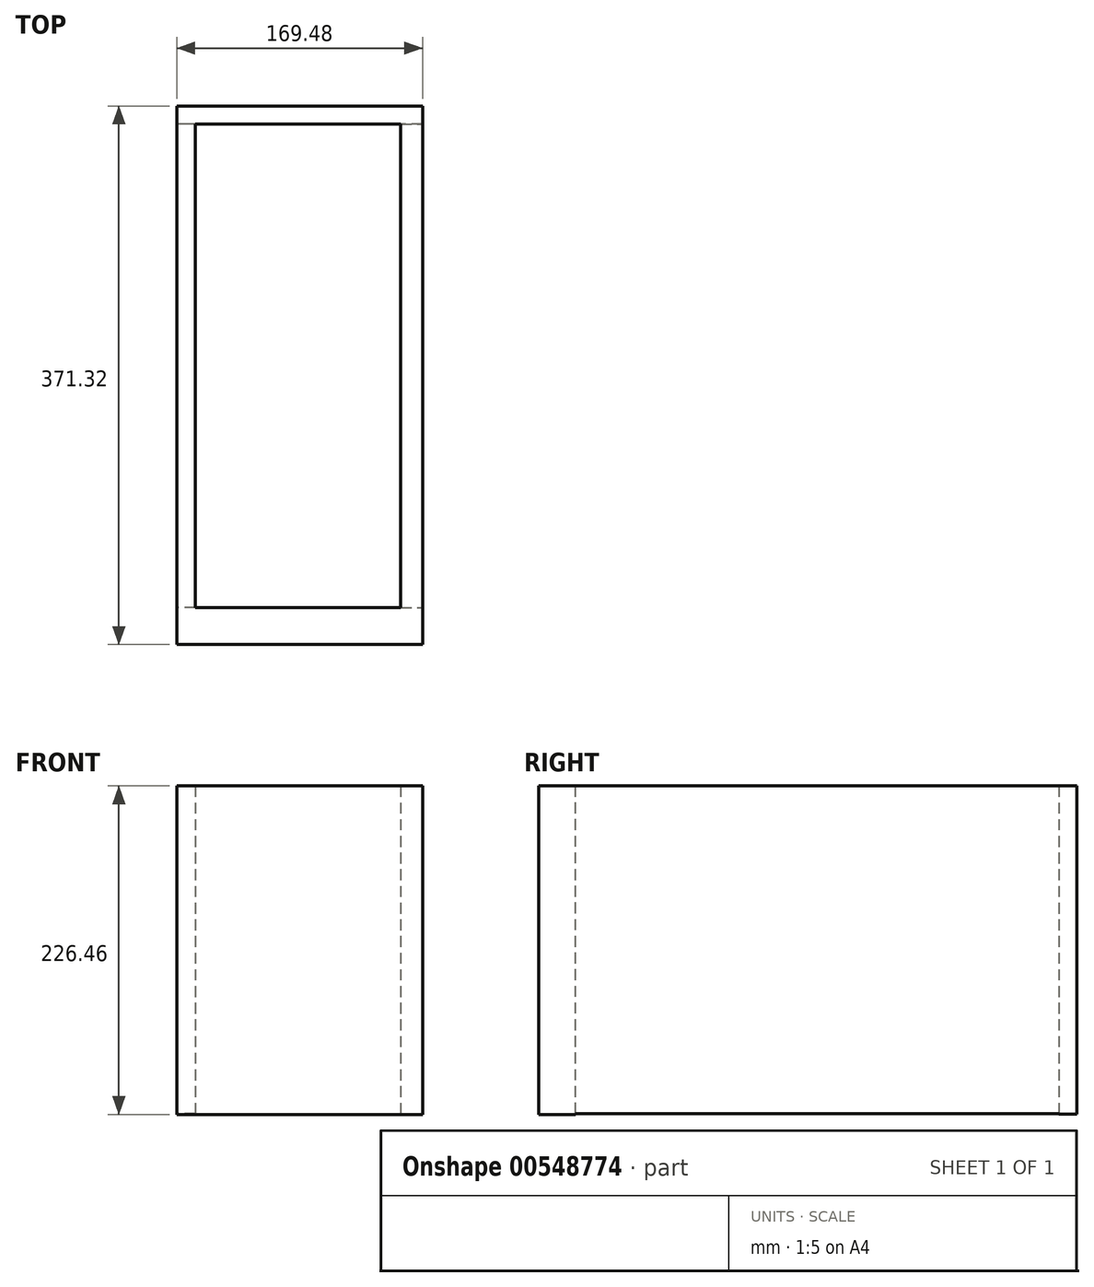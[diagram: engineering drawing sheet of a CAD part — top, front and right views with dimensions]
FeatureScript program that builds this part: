
annotation { "Feature Type Name" : "Feature", "Feature Type Description" : "" }
export const myFeature = defineFeature(function(context is Context, id is Id, definition is map)
    precondition{}
    {
        {
            var Q0;
            Q0=qCreatedBy(makeId("Front.planeOp"),FACE);
            var sketch = newSketch(context, id + "F0", { "sketchPlane" : qUnion([Q0])});
            skLineSegment(sketch, "E0.bottom", {"start": v(-84.74, -113.23) * mm, "end": v(84.74, -113.23) * mm});
            skLineSegment(sketch, "E0.top", {"start": v(-84.74, 113.23) * mm, "end": v(84.74, 113.23) * mm});
            skLineSegment(sketch, "E0.left", {"start": v(-84.74, -113.23) * mm, "end": v(-84.74, 113.23) * mm});
            skLineSegment(sketch, "E0.right", {"start": v(84.74, -113.23) * mm, "end": v(84.74, 113.23) * mm});
            skPoint(sketch, "E0.middle", {"position": v(0, 0) * mm});
            skSolve(sketch);
        }
        {
            var Q0;
            Q0=makeQuery(id+"F0.imprint","IMPRINT",FACE,{"disambiguationData":[TD([[makeQuery(id+"F0.imprint","IMPRINT",EDGE,{"derivedFrom":sQuery(id+"F0.wireOp",EDGE,"E0.bottom")}),1.0]])]});
            extrude(context, id + "F1", {"entities" : qUnion([Q0]), "depth" : 25.4 * mm, "offsetDistance" : 25.4 * mm});
        }
        {
            var Q0;
            Q0=makeQuery(id+"F1.opExtrude","SWEPT_FACE",FACE,{"disambiguationData":[OSD([sQuery(id+"F0.wireOp",EDGE,"E0.right")])]});
            var sketch = newSketch(context, id + "F2", { "sketchPlane" : qUnion([Q0])});
            skLineSegment(sketch, "E1.bottom", {"start": v(0, 113.23) * mm, "end": v(345.92, 113.23) * mm});
            skLineSegment(sketch, "E1.top", {"start": v(0, -112.63) * mm, "end": v(345.92, -112.63) * mm});
            skLineSegment(sketch, "E1.left", {"start": v(0, 113.23) * mm, "end": v(0, -112.63) * mm});
            skLineSegment(sketch, "E1.right", {"start": v(345.92, 113.23) * mm, "end": v(345.92, -112.63) * mm});
            skSolve(sketch);
        }
        {
            var Q0;
            Q0=makeQuery(id+"F1.opExtrude","SWEPT_FACE",FACE,{"disambiguationData":[OSD([sQuery(id+"F0.wireOp",EDGE,"E0.left")])]});
            var sketch = newSketch(context, id + "F3", { "sketchPlane" : qUnion([Q0])});
            skLineSegment(sketch, "E2.bottom", {"start": v(25.4, 113.23) * mm, "end": v(-345.58, 113.23) * mm});
            skLineSegment(sketch, "E2.top", {"start": v(25.4, -112.66) * mm, "end": v(-345.58, -112.66) * mm});
            skLineSegment(sketch, "E2.left", {"start": v(25.4, 113.23) * mm, "end": v(25.4, -112.66) * mm});
            skLineSegment(sketch, "E2.right", {"start": v(-345.58, 113.23) * mm, "end": v(-345.58, -112.66) * mm});
            skSolve(sketch);
        }
        {
            var Q0;
            {var subQ3=sQuery(id+"F3.wireOp",EDGE,"E2.right");Q0=makeQuery(id+"F3.imprint","IMPRINT",FACE,{"disambiguationData":[TD([[makeQuery(id+"F3.imprint","IMPRINT",EDGE,{"derivedFrom":subQ3}),1.0]])]});}
            extrude(context, id + "F4", {"entities" : qUnion([Q0]), "operationType" : NewBodyOperationType.ADD, "oppositeDirection" : true, "depth" : 12.88 * mm, "offsetDistance" : 25.4 * mm});
        }
        {
            var Q0;
            Q0=makeQuery(id+"F2.imprint","IMPRINT",FACE,{"disambiguationData":[TD([[makeQuery(id+"F2.imprint","IMPRINT",EDGE,{"derivedFrom":sQuery(id+"F2.wireOp",EDGE,"E1.bottom")}),-1.0]])]});
            extrude(context, id + "F5", {"entities" : qUnion([Q0]), "operationType" : NewBodyOperationType.ADD, "oppositeDirection" : true, "depth" : 15.04 * mm, "offsetDistance" : 25.4 * mm});
        }
        {
            var Q0;
            Q0=makeQuery(id+"F5.opExtrude","SWEPT_FACE",FACE,{"disambiguationData":[OSD([sQuery(id+"F2.wireOp",EDGE,"E1.right")])]});
            var sketch = newSketch(context, id + "F6", { "sketchPlane" : qUnion([Q0])});
            skLineSegment(sketch, "E3.bottom", {"start": v(-84.74, 113.23) * mm, "end": v(84.54, 113.23) * mm});
            skLineSegment(sketch, "E3.top", {"start": v(-84.74, -113.1) * mm, "end": v(84.54, -113.1) * mm});
            skLineSegment(sketch, "E3.left", {"start": v(-84.74, 113.23) * mm, "end": v(-84.74, -113.1) * mm});
            skLineSegment(sketch, "E3.right", {"start": v(84.54, 113.23) * mm, "end": v(84.54, -113.1) * mm});
            skSolve(sketch);
        }
        {
            var Q0;
            {var subQ3=sQuery(id+"F6.wireOp",EDGE,"E3.top");Q0=makeQuery(id+"F6.imprint","IMPRINT",FACE,{"disambiguationData":[TD([[makeQuery(id+"F6.imprint","IMPRINT",EDGE,{"derivedFrom":subQ3}),1.0]])]});}
            extrude(context, id + "F7", {"entities" : qUnion([Q0]), "operationType" : NewBodyOperationType.ADD, "oppositeDirection" : true, "depth" : 12.4 * mm, "offsetDistance" : 25.4 * mm});
        }
    });
